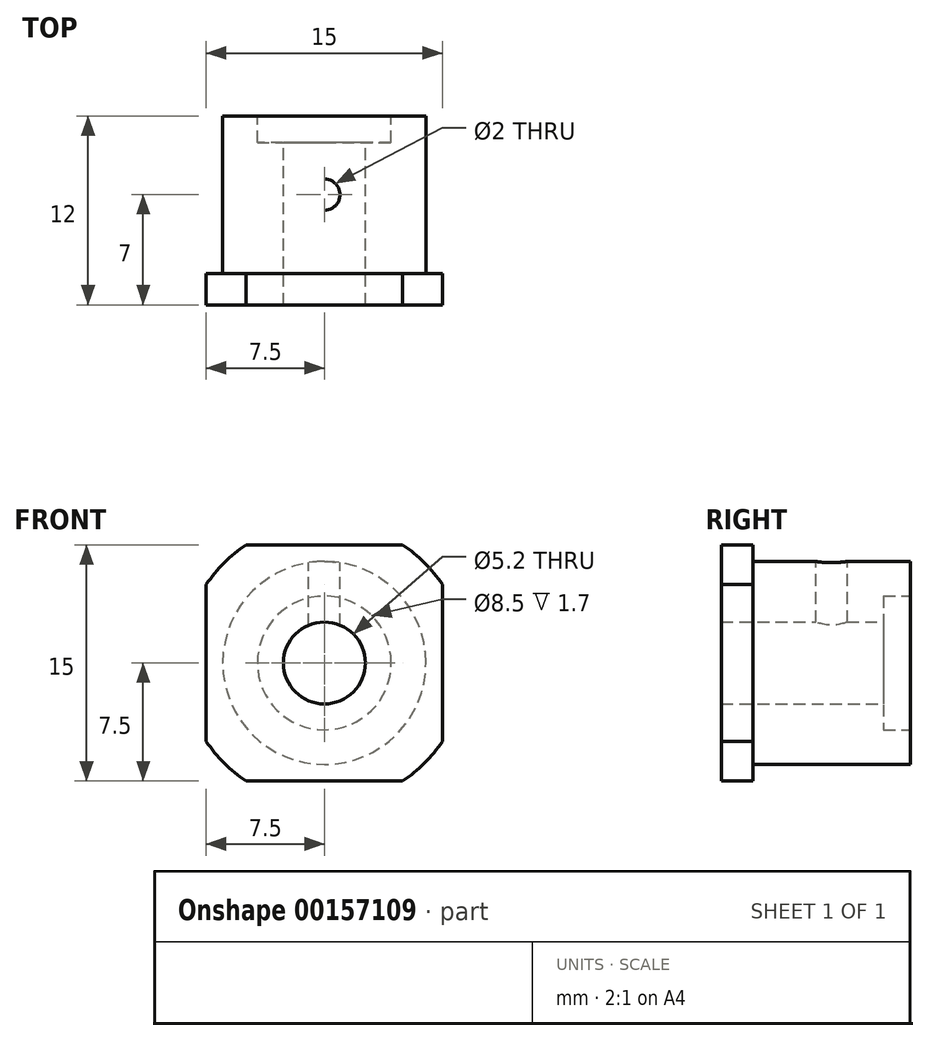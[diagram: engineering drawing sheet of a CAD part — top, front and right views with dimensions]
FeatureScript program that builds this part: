
annotation { "Feature Type Name" : "Feature", "Feature Type Description" : "" }
export const myFeature = defineFeature(function(context is Context, id is Id, definition is map)
    precondition{}
    {
        {
            assignVariable(context, id + "F0", {"name" : "OutDiam_Main", "anyValue" : 12.9});
        }
        {
            assignVariable(context, id + "F1", {"name" : "InDiam_Bore", "anyValue" : 2});
        }
        {
            assignVariable(context, id + "F2", {"name" : "Length_Square", "anyValue" : 2});
        }
        {
            assignVariable(context, id + "F3", {"name" : "Height_Square", "anyValue" : 15});
        }
        {
            var Q0;
            Q0=qCreatedBy(makeId("Right.planeOp"),FACE);
            var sketch = newSketch(context, id + "F4", { "sketchPlane" : qUnion([Q0])});
            skLineSegment(sketch, "E0", {"start": v(12.22, 0) * mm, "end": v(0, 0) * mm, "construction": true});
            skLineSegment(sketch, "E1", {"start": v(8.3, 2.6) * mm, "end": v(0, 2.6) * mm});
            skLineSegment(sketch, "E2", {"start": v(8.3, 2.6) * mm, "end": v(8.3, 4.25) * mm});
            skLineSegment(sketch, "E3", {"start": v(10, 4.25) * mm, "end": v(8.3, 4.25) * mm});
            skLineSegment(sketch, "E4", {"start": v(10, 4.25) * mm, "end": v(10, 6.45) * mm});
            skLineSegment(sketch, "E5", {"start": v(0, 6.45) * mm, "end": v(10, 6.45) * mm});
            skLineSegment(sketch, "E6", {"start": v(0, 6.45) * mm, "end": v(0, 2.6) * mm});
            skSolve(sketch);
        }
        {
            var Q0;
            Q0=makeQuery(id+"F4.imprint","IMPRINT",FACE,{"disambiguationData":[TD([[makeQuery(id+"F4.imprint","IMPRINT",EDGE,{"derivedFrom":sQuery(id+"F4.wireOp",EDGE,"E1")}),-1.0]])]});
            var Q1;
            Q1=sQuery(id+"F4.wireOp",EDGE,"E0");
            revolve(context, id + "F5", {"entities" : qUnion([Q0]), "axis" : qUnion([Q1]), "revolveType" : RevolveType.FULL});
        }
        {
            var Q0;
            Q0=makeQuery(id+"F5.opRevolve","SWEPT_FACE",FACE,{"disambiguationData":[OSD([sQuery(id+"F4.wireOp",EDGE,"E6")])]});
            var sketch = newSketch(context, id + "F6", { "sketchPlane" : qUnion([Q0])});
            skCircle(sketch, "E7.0", {"center": v(0, 0) * mm, "radius": 2.6 * mm});
            skLineSegment(sketch, "E8.bottom", {"start": v(7.5, 7.5) * mm, "end": v(-7.5, 7.5) * mm});
            skLineSegment(sketch, "E8.top", {"start": v(7.5, -7.5) * mm, "end": v(-7.5, -7.5) * mm});
            skLineSegment(sketch, "E8.left", {"start": v(7.5, 7.5) * mm, "end": v(7.5, -7.5) * mm});
            skLineSegment(sketch, "E8.right", {"start": v(-7.5, 7.5) * mm, "end": v(-7.5, -7.5) * mm});
            skCircle(sketch, "E9", {"center": v(0, 0) * mm, "radius": 9 * mm});
            skSolve(sketch);
        }
        {
            var Q0;
            Q0=makeQuery(id+"F6.imprint","IMPRINT",FACE,{"disambiguationData":[TD([[makeQuery(id+"F6.imprint","IMPRINT",EDGE,{"derivedFrom":makeQuery(id+"F5.opRevolve","SWEPT_EDGE",EDGE,{"disambiguationData":[OSD([sQuery(id+"F4.wireOp",EDGE,"E5"),sQuery(id+"F4.wireOp",EDGE,"E6")])]})}),1.0]])]});
            var Q1;
            Q1=makeQuery(id+"F6.imprint","IMPRINT",FACE,{"disambiguationData":[TD([[makeQuery(id+"F6.imprint","IMPRINT",EDGE,{"derivedFrom":sQuery(id+"F6.wireOp",EDGE,"E7.0")}),1.0]])]});
            extrude(context, id + "F7", {"entities" : qUnion([Q0, Q1]), "operationType" : NewBodyOperationType.ADD, "depth" : (getVariable(context, 'Length_Square')) * mm});
        }
        {
            var Q0;
            Q0=makeQuery(id+"F7.opExtrude","SWEPT_FACE",FACE,{"disambiguationData":[OSD([sQuery(id+"F6.wireOp",EDGE,"E8.bottom")])]});
            var sketch = newSketch(context, id + "F8", { "sketchPlane" : qUnion([Q0])});
            skLineSegment(sketch, "E10", {"start": v(6.45, 10) * mm, "end": v(6.45, 0) * mm});
            skLineSegment(sketch, "E11", {"start": v(-6.45, 0) * mm, "end": v(-6.45, 10) * mm});
            skPoint(sketch, "E12", {"position": v(0, 5) * mm});
            skSolve(sketch);
        }
        {
            var Q0;
            Q0=sQuery(id+"F8.wireOp",VERTEX,"E12");
            var Q1;
            Q1=makeQuery(id+"F5.opRevolve","SWEPT_BODY",BODY,{"disambiguationData":[OSD([sQuery(id+"F4.wireOp",EDGE,"E1"),sQuery(id+"F4.wireOp",EDGE,"E2"),sQuery(id+"F4.wireOp",EDGE,"E3"),sQuery(id+"F4.wireOp",EDGE,"E4"),sQuery(id+"F4.wireOp",EDGE,"E5"),sQuery(id+"F4.wireOp",EDGE,"E6")])]});
            hole(context, id + "F9", {"style" : HoleStyle.C_SINK, "endStyle" : HoleEndStyle.BLIND, "holeDiameter" : (getVariable(context, 'InDiam_Bore')) * mm, "cSinkDiameter" : (getVariable(context, 'Height_Square') - getVariable(context, 'OutDiam_Main') + 0.5) * mm, "cSinkAngle" : 90 * degree, "holeDepth" : (getVariable(context, 'OutDiam_Main') / 2) * mm, "startFromSketch" : true, "locations" : qUnion([Q0]), "scope" : qUnion([Q1])});
        }
    });
